# Revit family: Outdoor-Kitchen-Cabinets_Kalamazoo_Grill-Surrounds_Signature1
name_source: partatom
category: Specialty Equipment
revit_build: Autodesk Revit 2018 (Build: 20190510_1515(x64)
units: mm (PartAtom-declared; Revit-internal decimal feet)

## family parameters
Always vertical = Yes
Cut with Voids When Loaded = No
OmniClass Number = 23.40.40.11
OmniClass Title = Specialized Food Storage and Display Furnishings
Part Type = Normal
Room Calculation Point = No
Round Connector Dimension = Use Diameter
Shared = No
Work Plane-Based = No

## types (4) — shared parameters
Assembly Code = E1090310
Depth = 30"
Edition number = 1
Keynote = 11400
Manufacturer = Kalamazoo Outdoor Gourmet
Product Guid = d20acd5e-0c06-401e-b3b6-0332ecc75748
Product Material = Kalamazoo - Stainless Steel - 304 OR 316L
Product data url = https://www.bimobject.com
URL = https://kalamazoogourmet.com
Ι_Gnrc Mdl Optn 01 = Extension : +3/4"
Ι_Gnrc Mdl Optn 02 = Extension : -3/4"

## per-type parameters (varying)
| type | Description | I_K-SURR-1000 | Weight (lb) | Width |
| K-SURR-500 | Signature K500HB Grill Surround | No | 240.00 lbf | 36" |
| K-SURR-750G | Signature K750GB Grill Surround | Yes | 255.00 lbf | 50" |
| K-SURR-750H | Signature K750HB Grill Surround | Yes | 255.00 lbf | 46" |
| K-SURR-1000 | Signature K1000HB Grill Surround | Yes | 315.00 lbf | 59" |

note: column(s) folded — value = type name in every type: Model

## geometry (parser evidence)
native form markers: Sweep x6
no freeform markers — native parametric forms only
